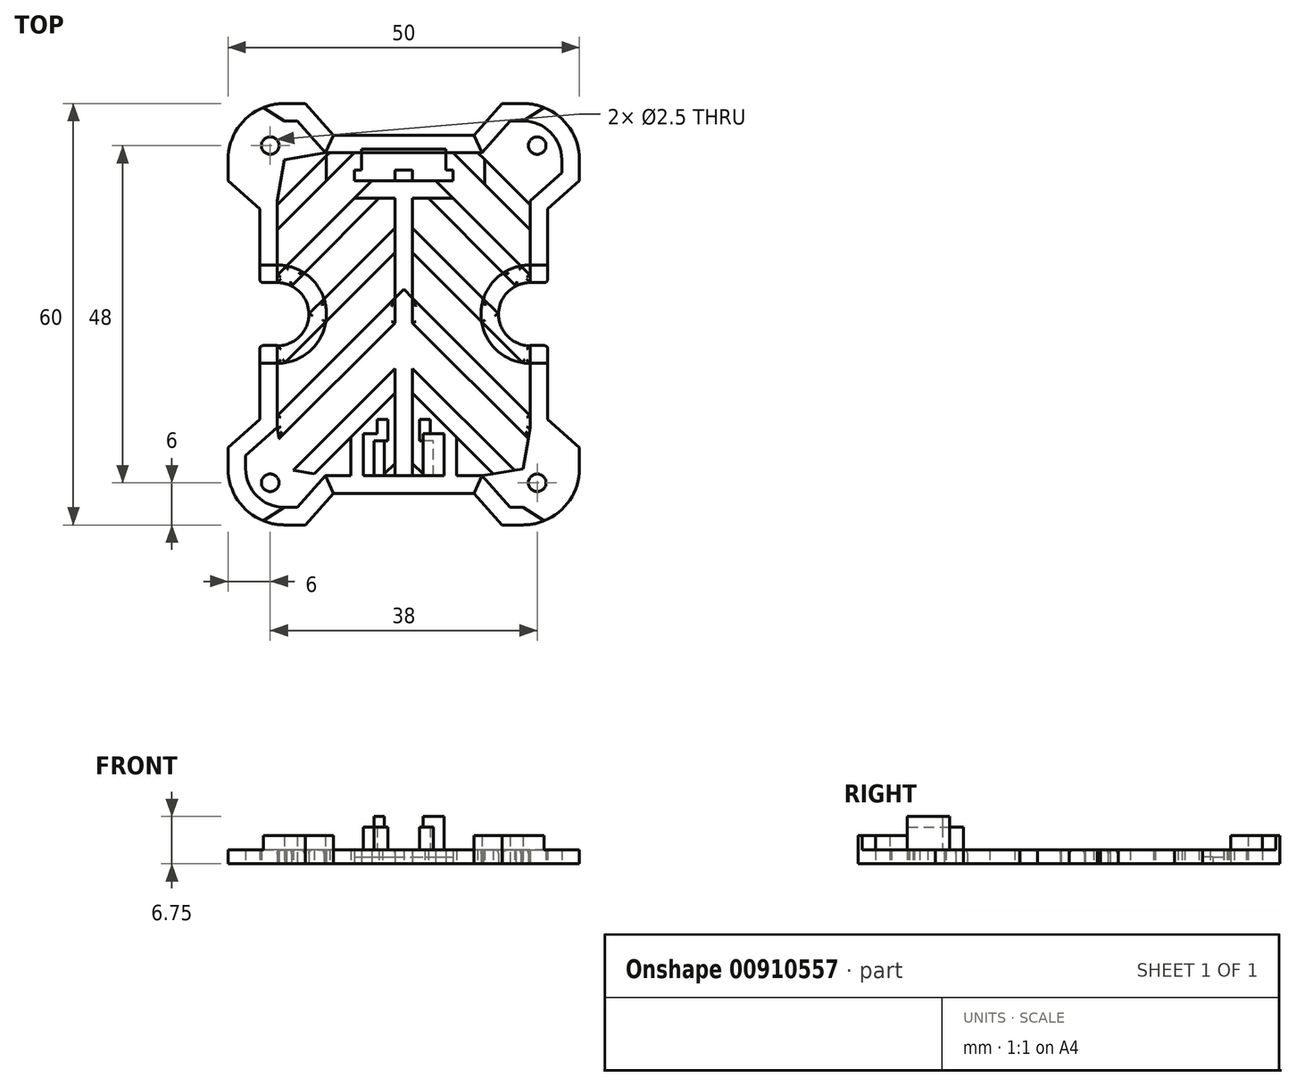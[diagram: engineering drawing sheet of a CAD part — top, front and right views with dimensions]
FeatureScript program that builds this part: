
annotation { "Feature Type Name" : "Feature", "Feature Type Description" : "" }
export const myFeature = defineFeature(function(context is Context, id is Id, definition is map)
    precondition{}
    {
        {
            var Q0;
            Q0=qCreatedBy(makeId("Top.planeOp"),FACE);
            var sketch = newSketch(context, id + "F0", { "sketchPlane" : qUnion([Q0])});
            skPoint(sketch, "E0.visualSharp", {"position": v(-25, 30) * mm});
            skArc(sketch, "E0.filletArc", {"start": v(-17, 30) * mm, "mid": v(-22.66, 27.66) * mm, "end": v(-25, 22) * mm});
            skPoint(sketch, "E1.visualSharp", {"position": v(25, 30) * mm});
            skArc(sketch, "E1.filletArc", {"start": v(25, 22) * mm, "mid": v(22.66, 27.66) * mm, "end": v(17, 30) * mm});
            skPoint(sketch, "E2.visualSharp", {"position": v(25, -30) * mm});
            skArc(sketch, "E2.filletArc", {"start": v(17, -30) * mm, "mid": v(22.66, -27.66) * mm, "end": v(25, -22) * mm});
            skPoint(sketch, "E3.visualSharp", {"position": v(-25, -30) * mm});
            skArc(sketch, "E3.filletArc", {"start": v(-25, -22) * mm, "mid": v(-22.66, -27.66) * mm, "end": v(-17, -30) * mm});
            skCircle(sketch, "E4", {"center": v(-19, 24) * mm, "radius": 1.25 * mm});
            skCircle(sketch, "E5.MirrorC", {"center": v(19, 24) * mm, "radius": 1.25 * mm});
            skCircle(sketch, "E6.MirrorC", {"center": v(19, -24) * mm, "radius": 1.25 * mm});
            skCircle(sketch, "E7.MirrorC", {"center": v(-19, -24) * mm, "radius": 1.25 * mm});
            skLineSegment(sketch, "E8", {"start": v(-10, 25.5) * mm, "end": v(10, 25.5) * mm});
            skLineSegment(sketch, "E9", {"start": v(-17, 30) * mm, "end": v(-14, 30) * mm});
            skLineSegment(sketch, "E10", {"start": v(-10, 25.5) * mm, "end": v(-14, 30) * mm});
            skLineSegment(sketch, "E11", {"start": v(10, 25.5) * mm, "end": v(14, 30) * mm});
            skLineSegment(sketch, "E12", {"start": v(-10, -25.5) * mm, "end": v(10, -25.5) * mm});
            skLineSegment(sketch, "E13", {"start": v(-17, -30) * mm, "end": v(-14, -30) * mm});
            skLineSegment(sketch, "E14", {"start": v(14, 30) * mm, "end": v(17, 30) * mm});
            skLineSegment(sketch, "E15", {"start": v(-14, -30) * mm, "end": v(-10, -25.5) * mm});
            skLineSegment(sketch, "E16", {"start": v(17, -30) * mm, "end": v(14, -30) * mm});
            skLineSegment(sketch, "E17", {"start": v(14, -30) * mm, "end": v(10, -25.5) * mm});
            skLineSegment(sketch, "E18", {"start": v(-25, -22) * mm, "end": v(-25, -19) * mm});
            skLineSegment(sketch, "E19", {"start": v(-25, 22) * mm, "end": v(-25, 19) * mm});
            skLineSegment(sketch, "E20", {"start": v(25, 22) * mm, "end": v(25, 19) * mm});
            skLineSegment(sketch, "E21", {"start": v(25, -22) * mm, "end": v(25, -19) * mm});
            skLineSegment(sketch, "E22", {"start": v(-20.5, -15) * mm, "end": v(-20.5, 15) * mm});
            skLineSegment(sketch, "E23", {"start": v(-25, -19) * mm, "end": v(-20.5, -15) * mm});
            skLineSegment(sketch, "E24", {"start": v(-20.5, 15) * mm, "end": v(-25, 19) * mm});
            skLineSegment(sketch, "E25", {"start": v(20.5, -15) * mm, "end": v(20.5, 15) * mm});
            skLineSegment(sketch, "E26", {"start": v(20.5, 15) * mm, "end": v(25, 19) * mm});
            skLineSegment(sketch, "E27", {"start": v(20.5, -15) * mm, "end": v(25, -19) * mm});
            skLineSegment(sketch, "E28", {"start": v(-10, -25.5) * mm, "end": v(-20.5, -15) * mm, "construction": true});
            skLineSegment(sketch, "E29", {"start": v(10, -25.5) * mm, "end": v(20.5, -15) * mm, "construction": true});
            skLineSegment(sketch, "E30", {"start": v(-20.5, 15) * mm, "end": v(-10, 25.5) * mm, "construction": true});
            skLineSegment(sketch, "E31", {"start": v(20.5, 15) * mm, "end": v(10, 25.5) * mm, "construction": true});
            skLineSegment(sketch, "E32.0", {"start": v(-11.12, 23) * mm, "end": v(-15.12, 27.5) * mm});
            skLineSegment(sketch, "E32.1", {"start": v(17, -27.5) * mm, "end": v(15.12, -27.5) * mm});
            skArc(sketch, "E32.2", {"start": v(17, -27.5) * mm, "mid": v(20.89, -25.89) * mm, "end": v(22.5, -22) * mm});
            skLineSegment(sketch, "E32.3", {"start": v(22.5, -22) * mm, "end": v(22.5, -20.12) * mm});
            skLineSegment(sketch, "E32.4", {"start": v(18, -16.12) * mm, "end": v(22.5, -20.12) * mm});
            skLineSegment(sketch, "E32.5", {"start": v(18, -16.12) * mm, "end": v(18, 16.12) * mm});
            skLineSegment(sketch, "E32.6", {"start": v(18, 16.12) * mm, "end": v(22.5, 20.12) * mm});
            skLineSegment(sketch, "E32.7", {"start": v(11.12, 23) * mm, "end": v(15.12, 27.5) * mm});
            skLineSegment(sketch, "E32.8", {"start": v(15.12, 27.5) * mm, "end": v(17, 27.5) * mm});
            skArc(sketch, "E32.9", {"start": v(22.5, 22) * mm, "mid": v(20.89, 25.89) * mm, "end": v(17, 27.5) * mm});
            skLineSegment(sketch, "E32.10", {"start": v(22.5, 22) * mm, "end": v(22.5, 20.12) * mm});
            skLineSegment(sketch, "E32.11", {"start": v(15.12, -27.5) * mm, "end": v(11.12, -23) * mm});
            skLineSegment(sketch, "E32.12", {"start": v(-11.12, 23) * mm, "end": v(11.12, 23) * mm});
            skLineSegment(sketch, "E32.13", {"start": v(-11.12, -23) * mm, "end": v(11.12, -23) * mm});
            skLineSegment(sketch, "E32.14", {"start": v(-15.12, -27.5) * mm, "end": v(-11.12, -23) * mm});
            skLineSegment(sketch, "E32.15", {"start": v(-17, -27.5) * mm, "end": v(-15.12, -27.5) * mm});
            skArc(sketch, "E32.16", {"start": v(-22.5, -22) * mm, "mid": v(-20.89, -25.89) * mm, "end": v(-17, -27.5) * mm});
            skLineSegment(sketch, "E32.17", {"start": v(-22.5, -22) * mm, "end": v(-22.5, -20.12) * mm});
            skLineSegment(sketch, "E32.18", {"start": v(-22.5, -20.12) * mm, "end": v(-18, -16.12) * mm});
            skLineSegment(sketch, "E32.19", {"start": v(-18, -16.12) * mm, "end": v(-18, 16.12) * mm});
            skLineSegment(sketch, "E32.20", {"start": v(-18, 16.12) * mm, "end": v(-22.5, 20.12) * mm});
            skLineSegment(sketch, "E32.21", {"start": v(-22.5, 22) * mm, "end": v(-22.5, 20.12) * mm});
            skArc(sketch, "E32.22", {"start": v(-17, 27.5) * mm, "mid": v(-20.89, 25.89) * mm, "end": v(-22.5, 22) * mm});
            skLineSegment(sketch, "E32.23", {"start": v(-17, 27.5) * mm, "end": v(-15.12, 27.5) * mm});
            skLineSegment(sketch, "E33", {"start": v(-18, 16.12) * mm, "end": v(-17, 22) * mm});
            skLineSegment(sketch, "E34", {"start": v(-11.12, 23) * mm, "end": v(-17, 22) * mm});
            skLineSegment(sketch, "E35", {"start": v(11.12, 23) * mm, "end": v(17, 22) * mm});
            skLineSegment(sketch, "E36", {"start": v(18, 16.12) * mm, "end": v(17, 22) * mm});
            skLineSegment(sketch, "E37", {"start": v(-11.12, -23) * mm, "end": v(-17, -22) * mm});
            skLineSegment(sketch, "E38", {"start": v(-18, -16.12) * mm, "end": v(-17, -22) * mm});
            skLineSegment(sketch, "E39", {"start": v(11.12, -23) * mm, "end": v(17, -22) * mm});
            skLineSegment(sketch, "E40", {"start": v(18, -16.12) * mm, "end": v(17, -22) * mm});
            skLineSegment(sketch, "E41", {"start": v(0, 3.54) * mm, "end": v(-18, -14.46) * mm});
            skLineSegment(sketch, "E42", {"start": v(0, 3.54) * mm, "end": v(18, -14.46) * mm});
            skLineSegment(sketch, "E43.0", {"start": v(-1.25, -1.25) * mm, "end": v(-17.75, -17.75) * mm});
            skLineSegment(sketch, "E43.1", {"start": v(1.25, -1.25) * mm, "end": v(17.75, -17.75) * mm});
            skLineSegment(sketch, "E44.0.1.0", {"start": v(1.25, 12.29) * mm, "end": v(18, -4.46) * mm});
            skLineSegment(sketch, "E44.0.1.1", {"start": v(1.25, 8.75) * mm, "end": v(18, -8) * mm});
            skLineSegment(sketch, "E44.0.1.2", {"start": v(-1.25, 8.75) * mm, "end": v(-18, -8) * mm});
            skLineSegment(sketch, "E44.0.1.3", {"start": v(-1.25, 12.29) * mm, "end": v(-18, -4.46) * mm});
            skLineSegment(sketch, "E44.0.2.0", {"start": v(1.25, 22.29) * mm, "end": v(18, 5.54) * mm});
            skLineSegment(sketch, "E44.0.2.1", {"start": v(1.25, 18.75) * mm, "end": v(18, 2) * mm});
            skLineSegment(sketch, "E44.0.2.2", {"start": v(-1.25, 18.75) * mm, "end": v(-18, 2) * mm});
            skLineSegment(sketch, "E44.0.2.3", {"start": v(-1.25, 22.29) * mm, "end": v(-18, 5.54) * mm});
            skLineSegment(sketch, "E44.0.3.2", {"start": v(-7, 23) * mm, "end": v(-18, 12) * mm});
            skLineSegment(sketch, "E44.0.3.3", {"start": v(-10.54, 23) * mm, "end": v(-18, 15.54) * mm});
            skLineSegment(sketch, "E44.direction1", {"start": v(18, -14.46) * mm, "end": v(43, -14.46) * mm, "construction": true});
            skLineSegment(sketch, "E44.direction2", {"start": v(18, -14.46) * mm, "end": v(18, -4.46) * mm, "construction": true});
            skLineSegment(sketch, "E45.0.1.0", {"start": v(1.25, -11.25) * mm, "end": v(12.75, -22.75) * mm});
            skLineSegment(sketch, "E45.0.1.1", {"start": v(1.25, -7.71) * mm, "end": v(15.75, -22.21) * mm});
            skLineSegment(sketch, "E45.0.1.2", {"start": v(-1.25, -7.71) * mm, "end": v(-15.75, -22.21) * mm});
            skLineSegment(sketch, "E45.0.1.3", {"start": v(-1.25, -11.25) * mm, "end": v(-12.75, -22.75) * mm});
            skLineSegment(sketch, "E45.0.2.0", {"start": v(1.25, -21.25) * mm, "end": v(3, -23) * mm});
            skLineSegment(sketch, "E45.0.2.1", {"start": v(1.25, -17.71) * mm, "end": v(6.54, -23) * mm});
            skLineSegment(sketch, "E45.0.2.2", {"start": v(-1.25, -17.71) * mm, "end": v(-6.54, -23) * mm});
            skLineSegment(sketch, "E45.0.2.3", {"start": v(-1.25, -21.25) * mm, "end": v(-3, -23) * mm});
            skLineSegment(sketch, "E45.direction1", {"start": v(18, -18) * mm, "end": v(43, -18) * mm, "construction": true});
            skLineSegment(sketch, "E45.direction2", {"start": v(18, -18) * mm, "end": v(18, -28) * mm, "construction": true});
            skPoint(sketch, "E46.orphan", {"position": v(-18, -34.46) * mm});
            skPoint(sketch, "E47.orphan", {"position": v(-18, -38) * mm});
            skPoint(sketch, "E48.orphan", {"position": v(18, -34.46) * mm});
            skLineSegment(sketch, "E49.trimOffspring", {"start": v(7, 23) * mm, "end": v(18, 12) * mm});
            skLineSegment(sketch, "E50.trimOffspring", {"start": v(10.54, 23) * mm, "end": v(18, 15.54) * mm});
            skPoint(sketch, "E51.orphan", {"position": v(0, 30) * mm});
            skPoint(sketch, "E52.orphan", {"position": v(0, 33.54) * mm});
            skPoint(sketch, "E53.orphan", {"position": v(0, 23.54) * mm});
            skLineSegment(sketch, "E54.bottom", {"start": v(-1.25, 23) * mm, "end": v(1.25, 23) * mm});
            skLineSegment(sketch, "E54.top", {"start": v(-1.25, -23) * mm, "end": v(1.25, -23) * mm});
            skLineSegment(sketch, "E54.left", {"start": v(-1.25, 23) * mm, "end": v(-1.25, -23) * mm});
            skLineSegment(sketch, "E54.right", {"start": v(1.25, 23) * mm, "end": v(1.25, -23) * mm});
            skPoint(sketch, "E54.middle", {"position": v(0, 0) * mm});
            skPoint(sketch, "E55.orphan", {"position": v(0, 20) * mm});
            skPoint(sketch, "E56.orphan", {"position": v(0, 13.54) * mm});
            skPoint(sketch, "E57.orphan", {"position": v(0, 10) * mm});
            skPoint(sketch, "E58.orphan", {"position": v(0, -20) * mm});
            skPoint(sketch, "E59.orphan", {"position": v(0, -16.46) * mm});
            skPoint(sketch, "E60.orphan", {"position": v(0, -10) * mm});
            skPoint(sketch, "E61.orphan", {"position": v(0, -6.46) * mm});
            skLineSegment(sketch, "E62", {"start": v(-7.5, -23) * mm, "end": v(-7.5, -17.5) * mm});
            skLineSegment(sketch, "E63.MirrorCS", {"start": v(7.5, -23) * mm, "end": v(7.5, -17.5) * mm});
            skLineSegment(sketch, "E64", {"start": v(-11.12, 23) * mm, "end": v(-10, 25.5) * mm});
            skLineSegment(sketch, "E65", {"start": v(-17, 27.5) * mm, "end": v(-20, 29.42) * mm});
            skLineSegment(sketch, "E66", {"start": v(11.12, 23) * mm, "end": v(10, 25.5) * mm});
            skLineSegment(sketch, "E67", {"start": v(17, 27.5) * mm, "end": v(20, 29.42) * mm});
            skLineSegment(sketch, "E68", {"start": v(-10, -25.5) * mm, "end": v(-11.12, -23) * mm});
            skLineSegment(sketch, "E69", {"start": v(10, -25.5) * mm, "end": v(11.12, -23) * mm});
            skLineSegment(sketch, "E70", {"start": v(-17, -27.5) * mm, "end": v(-20, -29.42) * mm});
            skLineSegment(sketch, "E71", {"start": v(17, -27.5) * mm, "end": v(20, -29.42) * mm});
            skArc(sketch, "E72.trimOffspring", {"start": v(-18, -7) * mm, "mid": v(-11, 0) * mm, "end": v(-18, 7) * mm});
            skArc(sketch, "E73.trimOffspring", {"start": v(-18, -4.5) * mm, "mid": v(-13.5, 0) * mm, "end": v(-18, 4.5) * mm});
            skLineSegment(sketch, "E74", {"start": v(-18, 7) * mm, "end": v(-20.5, 7) * mm});
            skLineSegment(sketch, "E75", {"start": v(-18, 4.5) * mm, "end": v(-20.5, 4.5) * mm});
            skLineSegment(sketch, "E76", {"start": v(-18, -7) * mm, "end": v(-20.5, -7) * mm});
            skLineSegment(sketch, "E77", {"start": v(-18, -4.46) * mm, "end": v(-20.5, -4.46) * mm});
            skArc(sketch, "E78.MirrorCS", {"start": v(18, -4.5) * mm, "mid": v(13.5, 0) * mm, "end": v(18, 4.5) * mm});
            skArc(sketch, "E79.MirrorCS", {"start": v(18, -7) * mm, "mid": v(11, 0) * mm, "end": v(18, 7) * mm});
            skLineSegment(sketch, "E80.MirrorCS", {"start": v(18, 4.5) * mm, "end": v(20.5, 4.5) * mm});
            skLineSegment(sketch, "E81.MirrorCS", {"start": v(18, 7) * mm, "end": v(20.5, 7) * mm});
            skLineSegment(sketch, "E82.MirrorCS", {"start": v(18, -7) * mm, "end": v(20.5, -7) * mm});
            skLineSegment(sketch, "E83.MirrorCS", {"start": v(18, -4.46) * mm, "end": v(20.5, -4.46) * mm});
            skLineSegment(sketch, "E84.bottom", {"start": v(-9, 20.5) * mm, "end": v(-7, 20.5) * mm});
            skLineSegment(sketch, "E84.top", {"start": v(-9, 19) * mm, "end": v(-7, 19) * mm});
            skLineSegment(sketch, "E84.left", {"start": v(-9, 20.5) * mm, "end": v(-9, 19) * mm});
            skLineSegment(sketch, "E84.right", {"start": v(-7, 20.5) * mm, "end": v(-7, 19) * mm});
            skPoint(sketch, "E84.middle", {"position": v(-8, 19.75) * mm});
            skLineSegment(sketch, "E85", {"start": v(-7, 20.5) * mm, "end": v(7, 20.5) * mm});
            skLineSegment(sketch, "E86", {"start": v(-7, 19) * mm, "end": v(7, 19) * mm});
            skLineSegment(sketch, "E87.bottom", {"start": v(7, 20.5) * mm, "end": v(9, 20.5) * mm});
            skLineSegment(sketch, "E87.top", {"start": v(7, 19) * mm, "end": v(9, 19) * mm});
            skLineSegment(sketch, "E87.left", {"start": v(7, 20.5) * mm, "end": v(7, 19) * mm});
            skLineSegment(sketch, "E87.right", {"start": v(9, 20.5) * mm, "end": v(9, 19) * mm});
            skLineSegment(sketch, "E88", {"start": v(7, 19.75) * mm, "end": v(0, 19.75) * mm, "construction": true});
            skLineSegment(sketch, "E89", {"start": v(0, 19.75) * mm, "end": v(-7, 19.75) * mm, "construction": true});
            skLineSegment(sketch, "E90.top", {"start": v(-11, 16.5) * mm, "end": v(11.5, 16.5) * mm});
            skLineSegment(sketch, "E90.left", {"start": v(-11, 23) * mm, "end": v(-11, 16.5) * mm});
            skLineSegment(sketch, "E90.right", {"start": v(11.5, 23) * mm, "end": v(11.5, 16.5) * mm});
            skPoint(sketch, "E90.middle", {"position": v(0, 19.75) * mm});
            skLineSegment(sketch, "E91.bottom", {"start": v(-6, 20.5) * mm, "end": v(6, 20.5) * mm});
            skLineSegment(sketch, "E91.top", {"start": v(-6, 23.5) * mm, "end": v(6, 23.5) * mm});
            skLineSegment(sketch, "E91.left", {"start": v(-6, 20.5) * mm, "end": v(-6, 23.5) * mm});
            skLineSegment(sketch, "E91.right", {"start": v(6, 20.5) * mm, "end": v(6, 23.5) * mm});
            skSolve(sketch);
        }
        {
            var Q0;
            Q0=makeQuery(id+"F0.imprint","IMPRINT",FACE,{"disambiguationData":[TD([[makeQuery(id+"F0.imprint","IMPRINT",EDGE,{"derivedFrom":sQuery(id+"F0.wireOp",EDGE,"qVhlgd7Z-K8wA-2s9c-4Va0-7I31SFR7jzgF.bottom")}),-1.0]])]});
            var Q1;
            {var subQ1=sQuery(id+"F0.wireOp",EDGE,"bAQaguaC-gw7z-6hSp-WNjj-it6Kwomhn3MH.bottom");var subQ4=sQuery(id+"F0.wireOp",EDGE,"bAQaguaC-gw7z-6hSp-WNjj-it6Kwomhn3MH.left");var subQ9=makeQuery(id+"F0.imprint","INTERSECT",VERTEX,{"derivedFrom":[subQ1,subQ4]});Q1=makeQuery(id+"F0.imprint","IMPRINT",FACE,{"disambiguationData":[TD([[makeQuery(id+"F0.imprint","IMPRINT",EDGE,{"disambiguationData":[TD([[subQ9,-1.0]])],"derivedFrom":subQ1}),-1.0]])]});}
            var Q2;
            {var subQ0=sQuery(id+"F0.wireOp",EDGE,"3b41a42e-ea02-44ec-bd11-05c8cb4d84110.MirrorCS");Q2=makeQuery(id+"F0.imprint","IMPRINT",FACE,{"disambiguationData":[TD([[makeQuery(id+"F0.imprint","IMPRINT",EDGE,{"derivedFrom":subQ0}),-1.0]])]});}
            var Q3;
            Q3=makeQuery(id+"F0.imprint","IMPRINT",FACE,{"disambiguationData":[TD([[makeQuery(id+"F0.imprint","IMPRINT",EDGE,{"derivedFrom":sQuery(id+"F0.wireOp",EDGE,"5EblEZfn-I8Wa-IbvZ-PO4Y-9xLoYuIDBuYk.bottom")}),-1.0]])]});
            var Q4;
            {var subQ0=sQuery(id+"F0.wireOp",EDGE,"252a318b-4038-41aa-b63b-639a4f701ae30.MirrorCS");Q4=makeQuery(id+"F0.imprint","IMPRINT",FACE,{"disambiguationData":[TD([[makeQuery(id+"F0.imprint","IMPRINT",EDGE,{"derivedFrom":subQ0}),1.0]])]});}
            var Q5;
            {var subQ0=sQuery(id+"F0.wireOp",EDGE,"58b98b9d-614e-4e5d-8269-9d4372af3b9f0.MirrorCS");Q5=makeQuery(id+"F0.imprint","IMPRINT",FACE,{"disambiguationData":[TD([[makeQuery(id+"F0.imprint","IMPRINT",EDGE,{"derivedFrom":subQ0}),-1.0]])]});}
            var Q6;
            Q6=makeQuery(id+"F0.imprint","IMPRINT",FACE,{"disambiguationData":[TD([[makeQuery(id+"F0.imprint","IMPRINT",EDGE,{"derivedFrom":sQuery(id+"F0.wireOp",EDGE,"E0.filletArc")}),1.0]])]});
            var Q7;
            Q7=makeQuery(id+"F0.imprint","IMPRINT",FACE,{"disambiguationData":[TD([[makeQuery(id+"F0.imprint","IMPRINT",EDGE,{"derivedFrom":sQuery(id+"F0.wireOp",EDGE,"xvgLrtku-wdkR-8HBo-YxuC-FjmSOnXhvL37")}),-1.0]])]});
            var Q8;
            Q8=makeQuery(id+"F0.imprint","IMPRINT",FACE,{"disambiguationData":[TD([[makeQuery(id+"F0.imprint","IMPRINT",EDGE,{"derivedFrom":sQuery(id+"F0.wireOp",EDGE,"E10")}),1.0]])]});
            var Q9;
            Q9=makeQuery(id+"F0.imprint","IMPRINT",FACE,{"disambiguationData":[TD([[makeQuery(id+"F0.imprint","IMPRINT",EDGE,{"derivedFrom":sQuery(id+"F0.wireOp",EDGE,"5909cff1-2e5d-4e63-b456-f55076b46f4d0.MirrorCS")}),-1.0]])]});
            var Q10;
            Q10=makeQuery(id+"F0.imprint","IMPRINT",FACE,{"disambiguationData":[TD([[makeQuery(id+"F0.imprint","IMPRINT",EDGE,{"derivedFrom":sQuery(id+"F0.wireOp",EDGE,"86012b31-d1bc-4a6e-bdbf-ee867ae8a5b00.MirrorCS")}),1.0]])]});
            var Q11;
            Q11=makeQuery(id+"F0.imprint","IMPRINT",FACE,{"disambiguationData":[TD([[makeQuery(id+"F0.imprint","IMPRINT",EDGE,{"derivedFrom":sQuery(id+"F0.wireOp",EDGE,"afaa9ab5-ff9c-4d97-af4b-f4bc579a4ab80.MirrorCS")}),-1.0]])]});
            var Q12;
            {var subQ0=sQuery(id+"F0.wireOp",EDGE,"E49.trimOffspring");Q12=makeQuery(id+"F0.imprint","IMPRINT",FACE,{"disambiguationData":[TD([[makeQuery(id+"F0.imprint","IMPRINT",EDGE,{"derivedFrom":subQ0}),1.0]])]});}
            var Q13;
            {var subQ0=sQuery(id+"F0.wireOp",EDGE,"E45.0.1.1");Q13=makeQuery(id+"F0.imprint","IMPRINT",FACE,{"disambiguationData":[TD([[makeQuery(id+"F0.imprint","IMPRINT",EDGE,{"derivedFrom":subQ0}),-1.0]])]});}
            var Q14;
            {var subQ1=sQuery(id+"F0.wireOp",EDGE,"E45.0.2.0");Q14=makeQuery(id+"F0.imprint","IMPRINT",FACE,{"disambiguationData":[TD([[makeQuery(id+"F0.imprint","IMPRINT",EDGE,{"derivedFrom":subQ1}),1.0]])]});}
            var Q15;
            {var subQ3=sQuery(id+"F0.wireOp",EDGE,"E41");Q15=makeQuery(id+"F0.imprint","IMPRINT",FACE,{"disambiguationData":[TD([[makeQuery(id+"F0.imprint","IMPRINT",EDGE,{"derivedFrom":subQ3}),1.0]])]});}
            var Q16;
            Q16=makeQuery(id+"F0.imprint","IMPRINT",FACE,{"disambiguationData":[TD([[makeQuery(id+"F0.imprint","IMPRINT",EDGE,{"derivedFrom":sQuery(id+"F0.wireOp",EDGE,"E6.MirrorC")}),-1.0]])]});
            var Q17;
            Q17=makeQuery(id+"F0.imprint","IMPRINT",FACE,{"disambiguationData":[TD([[makeQuery(id+"F0.imprint","IMPRINT",EDGE,{"derivedFrom":sQuery(id+"F0.wireOp",EDGE,"E5.MirrorC")}),1.0]])]});
            var Q18;
            Q18=makeQuery(id+"F0.imprint","IMPRINT",FACE,{"disambiguationData":[TD([[makeQuery(id+"F0.imprint","IMPRINT",EDGE,{"derivedFrom":sQuery(id+"F0.wireOp",EDGE,"E4")}),-1.0]])]});
            var Q19;
            Q19=makeQuery(id+"F0.imprint","IMPRINT",FACE,{"disambiguationData":[TD([[makeQuery(id+"F0.imprint","IMPRINT",EDGE,{"derivedFrom":sQuery(id+"F0.wireOp",EDGE,"E7.MirrorC")}),1.0]])]});
            var Q20;
            {var subQ13=sQuery(id+"F0.wireOp",EDGE,"E54.top");Q20=makeQuery(id+"F0.imprint","IMPRINT",FACE,{"disambiguationData":[TD([[makeQuery(id+"F0.imprint","IMPRINT",EDGE,{"derivedFrom":subQ13}),1.0]])]});}
            var Q21;
            {var subQ5=sQuery(id+"F0.wireOp",EDGE,"E42");var subQ6=sQuery(id+"F0.wireOp",EDGE,"E32.5");var subQ7=makeQuery(id+"F0.imprint","INTERSECT",VERTEX,{"derivedFrom":[subQ6,subQ5]});Q21=makeQuery(id+"F0.imprint","IMPRINT",FACE,{"disambiguationData":[TD([[makeQuery(id+"F0.imprint","IMPRINT",EDGE,{"disambiguationData":[TD([[subQ7,1.0]])],"derivedFrom":subQ5}),-1.0]])]});}
            var Q22;
            {var subQ0=sQuery(id+"F0.wireOp",EDGE,"E45.0.1.2");Q22=makeQuery(id+"F0.imprint","IMPRINT",FACE,{"disambiguationData":[TD([[makeQuery(id+"F0.imprint","IMPRINT",EDGE,{"derivedFrom":subQ0}),1.0]])]});}
            var Q23;
            {var subQ0=sQuery(id+"F0.wireOp",EDGE,"E45.0.2.2");Q23=makeQuery(id+"F0.imprint","IMPRINT",FACE,{"disambiguationData":[TD([[makeQuery(id+"F0.imprint","IMPRINT",EDGE,{"derivedFrom":subQ0}),1.0]])]});}
            var Q24;
            {var subQ0=sQuery(id+"F0.wireOp",EDGE,"E45.0.2.3");Q24=makeQuery(id+"F0.imprint","IMPRINT",FACE,{"disambiguationData":[TD([[makeQuery(id+"F0.imprint","IMPRINT",EDGE,{"derivedFrom":subQ0}),1.0]])]});}
            var Q25;
            {var subQ0=sQuery(id+"F0.wireOp",EDGE,"E45.0.2.0");Q25=makeQuery(id+"F0.imprint","IMPRINT",FACE,{"disambiguationData":[TD([[makeQuery(id+"F0.imprint","IMPRINT",EDGE,{"derivedFrom":subQ0}),-1.0]])]});}
            var Q26;
            {var subQ4=sQuery(id+"F0.wireOp",EDGE,"E45.0.2.1");Q26=makeQuery(id+"F0.imprint","IMPRINT",FACE,{"disambiguationData":[TD([[makeQuery(id+"F0.imprint","IMPRINT",EDGE,{"derivedFrom":subQ4}),1.0]])]});}
            var Q27;
            {var subQ4=sQuery(id+"F0.wireOp",EDGE,"E45.0.2.2");Q27=makeQuery(id+"F0.imprint","IMPRINT",FACE,{"disambiguationData":[TD([[makeQuery(id+"F0.imprint","IMPRINT",EDGE,{"derivedFrom":subQ4}),-1.0]])]});}
            var Q28;
            {var subQ11=sQuery(id+"F0.wireOp",EDGE,"E18");Q28=makeQuery(id+"F0.imprint","IMPRINT",FACE,{"disambiguationData":[TD([[makeQuery(id+"F0.imprint","IMPRINT",EDGE,{"derivedFrom":subQ11}),-1.0]])]});}
            var Q29;
            Q29=makeQuery(id+"F0.imprint","IMPRINT",FACE,{"disambiguationData":[TD([[makeQuery(id+"F0.imprint","IMPRINT",EDGE,{"derivedFrom":sQuery(id+"F0.wireOp",EDGE,"E8")}),-1.0]])]});
            var Q30;
            {var subQ0=sQuery(id+"F0.wireOp",EDGE,"E20");Q30=makeQuery(id+"F0.imprint","IMPRINT",FACE,{"disambiguationData":[TD([[makeQuery(id+"F0.imprint","IMPRINT",EDGE,{"derivedFrom":subQ0}),-1.0]])]});}
            var Q31;
            Q31=makeQuery(id+"F0.imprint","IMPRINT",FACE,{"disambiguationData":[TD([[makeQuery(id+"F0.imprint","IMPRINT",EDGE,{"derivedFrom":sQuery(id+"F0.wireOp",EDGE,"E12")}),1.0]])]});
            var Q32;
            Q32=makeQuery(id+"F0.imprint","IMPRINT",FACE,{"disambiguationData":[TD([[makeQuery(id+"F0.imprint","IMPRINT",EDGE,{"derivedFrom":sQuery(id+"F0.wireOp",EDGE,"E11")}),-1.0]])]});
            var Q33;
            {var subQ0=sQuery(id+"F0.wireOp",EDGE,"E16");Q33=makeQuery(id+"F0.imprint","IMPRINT",FACE,{"disambiguationData":[TD([[makeQuery(id+"F0.imprint","IMPRINT",EDGE,{"derivedFrom":subQ0}),-1.0]])]});}
            var Q34;
            {var subQ0=sQuery(id+"F0.wireOp",EDGE,"E13");Q34=makeQuery(id+"F0.imprint","IMPRINT",FACE,{"disambiguationData":[TD([[makeQuery(id+"F0.imprint","IMPRINT",EDGE,{"derivedFrom":subQ0}),1.0]])]});}
            var Q35;
            {var subQ3=sQuery(id+"F0.wireOp",EDGE,"E19");Q35=makeQuery(id+"F0.imprint","IMPRINT",FACE,{"disambiguationData":[TD([[makeQuery(id+"F0.imprint","IMPRINT",EDGE,{"derivedFrom":subQ3}),1.0]])]});}
            var Q36;
            {var subQ4=sQuery(id+"F0.wireOp",EDGE,"E21");Q36=makeQuery(id+"F0.imprint","IMPRINT",FACE,{"disambiguationData":[TD([[makeQuery(id+"F0.imprint","IMPRINT",EDGE,{"derivedFrom":subQ4}),1.0]])]});}
            var Q37;
            {var subQ0=sQuery(id+"F0.wireOp",EDGE,"E82.MirrorCS");Q37=makeQuery(id+"F0.imprint","IMPRINT",FACE,{"disambiguationData":[TD([[makeQuery(id+"F0.imprint","IMPRINT",EDGE,{"derivedFrom":subQ0}),1.0]])]});}
            var Q38;
            {var subQ0=sQuery(id+"F0.wireOp",EDGE,"E44.0.2.0");var subQ1=sQuery(id+"F0.wireOp",EDGE,"E32.5");var subQ2=makeQuery(id+"F0.imprint","INTERSECT",VERTEX,{"derivedFrom":[subQ1,subQ0]});Q38=makeQuery(id+"F0.imprint","IMPRINT",FACE,{"disambiguationData":[TD([[makeQuery(id+"F0.imprint","IMPRINT",EDGE,{"disambiguationData":[TD([[subQ2,1.0]])],"derivedFrom":subQ0}),1.0]])]});}
            var Q39;
            {var subQ1=sQuery(id+"F0.wireOp",EDGE,"E32.5");var subQ7=sQuery(id+"F0.wireOp",EDGE,"E44.0.2.0");var subQ8=makeQuery(id+"F0.imprint","INTERSECT",VERTEX,{"derivedFrom":[subQ1,subQ7]});Q39=makeQuery(id+"F0.imprint","IMPRINT",FACE,{"disambiguationData":[TD([[makeQuery(id+"F0.imprint","IMPRINT",EDGE,{"disambiguationData":[TD([[subQ8,1.0]])],"derivedFrom":subQ7}),-1.0]])]});}
            var Q40;
            {var subQ0=sQuery(id+"F0.wireOp",EDGE,"E79.MirrorCS");var subQ1=sQuery(id+"F0.wireOp",EDGE,"E44.0.1.0");var subQ2=makeQuery(id+"F0.imprint","INTERSECT",VERTEX,{"derivedFrom":[subQ1,subQ0]});Q40=makeQuery(id+"F0.imprint","IMPRINT",FACE,{"disambiguationData":[TD([[makeQuery(id+"F0.imprint","IMPRINT",EDGE,{"disambiguationData":[TD([[subQ2,-1.0]])],"derivedFrom":subQ1}),1.0]])]});}
            var Q41;
            {var subQ3=sQuery(id+"F0.wireOp",EDGE,"E44.0.1.0");var subQ5=sQuery(id+"F0.wireOp",EDGE,"E79.MirrorCS");var subQ9=makeQuery(id+"F0.imprint","INTERSECT",VERTEX,{"derivedFrom":[subQ3,subQ5]});Q41=makeQuery(id+"F0.imprint","IMPRINT",FACE,{"disambiguationData":[TD([[makeQuery(id+"F0.imprint","IMPRINT",EDGE,{"disambiguationData":[TD([[subQ9,-1.0]])],"derivedFrom":subQ3}),-1.0]])]});}
            var Q42;
            {var subQ0=sQuery(id+"F0.wireOp",EDGE,"E79.MirrorCS");var subQ1=sQuery(id+"F0.wireOp",EDGE,"E44.0.1.1");var subQ2=makeQuery(id+"F0.imprint","INTERSECT",VERTEX,{"disambiguationData":[OD(0.0)],"derivedFrom":[subQ1,subQ0]});Q42=makeQuery(id+"F0.imprint","IMPRINT",FACE,{"disambiguationData":[TD([[makeQuery(id+"F0.imprint","IMPRINT",EDGE,{"disambiguationData":[TD([[subQ2,-1.0]])],"derivedFrom":subQ1}),-1.0]])]});}
            var Q43;
            {var subQ0=sQuery(id+"F0.wireOp",EDGE,"E80.MirrorCS");Q43=makeQuery(id+"F0.imprint","IMPRINT",FACE,{"disambiguationData":[TD([[makeQuery(id+"F0.imprint","IMPRINT",EDGE,{"derivedFrom":subQ0}),1.0]])]});}
            var Q44;
            {var subQ0=sQuery(id+"F0.wireOp",EDGE,"E54.right");var subQ1=sQuery(id+"F0.wireOp",EDGE,"E44.0.1.0");var subQ2=makeQuery(id+"F0.imprint","INTERSECT",VERTEX,{"derivedFrom":[subQ1,subQ0]});Q44=makeQuery(id+"F0.imprint","IMPRINT",FACE,{"disambiguationData":[TD([[makeQuery(id+"F0.imprint","IMPRINT",EDGE,{"disambiguationData":[TD([[subQ2,-1.0]])],"derivedFrom":subQ1}),-1.0]])]});}
            var Q45;
            {var subQ0=sQuery(id+"F0.wireOp",EDGE,"E72.trimOffspring");var subQ1=sQuery(id+"F0.wireOp",EDGE,"E44.0.1.3");var subQ2=makeQuery(id+"F0.imprint","INTERSECT",VERTEX,{"derivedFrom":[subQ1,subQ0]});Q45=makeQuery(id+"F0.imprint","IMPRINT",FACE,{"disambiguationData":[TD([[makeQuery(id+"F0.imprint","IMPRINT",EDGE,{"disambiguationData":[TD([[subQ2,-1.0]])],"derivedFrom":subQ1}),-1.0]])]});}
            var Q46;
            {var subQ0=sQuery(id+"F0.wireOp",EDGE,"E74");Q46=makeQuery(id+"F0.imprint","IMPRINT",FACE,{"disambiguationData":[TD([[makeQuery(id+"F0.imprint","IMPRINT",EDGE,{"derivedFrom":subQ0}),1.0]])]});}
            var Q47;
            {var subQ0=sQuery(id+"F0.wireOp",EDGE,"E54.left");var subQ1=sQuery(id+"F0.wireOp",EDGE,"E44.0.1.2");var subQ2=makeQuery(id+"F0.imprint","INTERSECT",VERTEX,{"derivedFrom":[subQ1,subQ0]});Q47=makeQuery(id+"F0.imprint","IMPRINT",FACE,{"disambiguationData":[TD([[makeQuery(id+"F0.imprint","IMPRINT",EDGE,{"disambiguationData":[TD([[subQ2,-1.0]])],"derivedFrom":subQ1}),-1.0]])]});}
            var Q48;
            {var subQ0=sQuery(id+"F0.wireOp",EDGE,"E44.0.2.3");var subQ1=sQuery(id+"F0.wireOp",EDGE,"E32.19");var subQ2=makeQuery(id+"F0.imprint","INTERSECT",VERTEX,{"derivedFrom":[subQ1,subQ0]});Q48=makeQuery(id+"F0.imprint","IMPRINT",FACE,{"disambiguationData":[TD([[makeQuery(id+"F0.imprint","IMPRINT",EDGE,{"disambiguationData":[TD([[subQ2,1.0]])],"derivedFrom":subQ0}),-1.0]])]});}
            var Q49;
            {var subQ0=sQuery(id+"F0.wireOp",EDGE,"E72.trimOffspring");var subQ1=sQuery(id+"F0.wireOp",EDGE,"E44.0.1.2");var subQ2=makeQuery(id+"F0.imprint","INTERSECT",VERTEX,{"disambiguationData":[OD(0.0)],"derivedFrom":[subQ1,subQ0]});Q49=makeQuery(id+"F0.imprint","IMPRINT",FACE,{"disambiguationData":[TD([[makeQuery(id+"F0.imprint","IMPRINT",EDGE,{"disambiguationData":[TD([[subQ2,-1.0]])],"derivedFrom":subQ1}),1.0]])]});}
            var Q50;
            {var subQ0=sQuery(id+"F0.wireOp",EDGE,"E72.trimOffspring");var subQ1=sQuery(id+"F0.wireOp",EDGE,"E44.0.2.2");var subQ2=makeQuery(id+"F0.imprint","INTERSECT",VERTEX,{"derivedFrom":[subQ1,subQ0]});Q50=makeQuery(id+"F0.imprint","IMPRINT",FACE,{"disambiguationData":[TD([[makeQuery(id+"F0.imprint","IMPRINT",EDGE,{"disambiguationData":[TD([[subQ2,-1.0]])],"derivedFrom":subQ1}),-1.0]])]});}
            var Q51;
            {var subQ0=sQuery(id+"F0.wireOp",EDGE,"E72.trimOffspring");var subQ3=sQuery(id+"F0.wireOp",EDGE,"E44.0.1.2");var subQ10=makeQuery(id+"F0.imprint","INTERSECT",VERTEX,{"disambiguationData":[OD(0.0)],"derivedFrom":[subQ3,subQ0]});Q51=makeQuery(id+"F0.imprint","IMPRINT",FACE,{"disambiguationData":[TD([[makeQuery(id+"F0.imprint","IMPRINT",EDGE,{"disambiguationData":[TD([[subQ10,-1.0]])],"derivedFrom":subQ3}),-1.0]])]});}
            var Q52;
            {var subQ0=sQuery(id+"F0.wireOp",EDGE,"E76");Q52=makeQuery(id+"F0.imprint","IMPRINT",FACE,{"disambiguationData":[TD([[makeQuery(id+"F0.imprint","IMPRINT",EDGE,{"derivedFrom":subQ0}),-1.0]])]});}
            var Q53;
            {var subQ0=sQuery(id+"F0.wireOp",EDGE,"E90.top");var subQ1=sQuery(id+"F0.wireOp",EDGE,"E44.0.2.2");var subQ2=makeQuery(id+"F0.imprint","INTERSECT",VERTEX,{"derivedFrom":[subQ1,subQ0]});Q53=makeQuery(id+"F0.imprint","IMPRINT",FACE,{"disambiguationData":[TD([[makeQuery(id+"F0.imprint","IMPRINT",EDGE,{"disambiguationData":[TD([[subQ2,-1.0]])],"derivedFrom":subQ1}),-1.0]])]});}
            var Q54;
            {var subQ0=sQuery(id+"F0.wireOp",EDGE,"E90.top");var subQ1=sQuery(id+"F0.wireOp",EDGE,"E44.0.2.0");var subQ2=makeQuery(id+"F0.imprint","INTERSECT",VERTEX,{"derivedFrom":[subQ1,subQ0]});Q54=makeQuery(id+"F0.imprint","IMPRINT",FACE,{"disambiguationData":[TD([[makeQuery(id+"F0.imprint","IMPRINT",EDGE,{"disambiguationData":[TD([[subQ2,-1.0]])],"derivedFrom":subQ1}),-1.0]])]});}
            var Q55;
            {var subQ0=sQuery(id+"F0.wireOp",EDGE,"E49.trimOffspring");var subQ1=sQuery(id+"F0.wireOp",EDGE,"E32.5");var subQ2=makeQuery(id+"F0.imprint","INTERSECT",VERTEX,{"derivedFrom":[subQ1,subQ0]});Q55=makeQuery(id+"F0.imprint","IMPRINT",FACE,{"disambiguationData":[TD([[makeQuery(id+"F0.imprint","IMPRINT",EDGE,{"disambiguationData":[TD([[subQ2,-1.0]])],"derivedFrom":subQ1}),1.0]])]});}
            var Q56;
            {var subQ0=sQuery(id+"F0.wireOp",EDGE,"E44.0.3.2");var subQ1=sQuery(id+"F0.wireOp",EDGE,"E32.19");var subQ2=makeQuery(id+"F0.imprint","INTERSECT",VERTEX,{"derivedFrom":[subQ1,subQ0]});Q56=makeQuery(id+"F0.imprint","IMPRINT",FACE,{"disambiguationData":[TD([[makeQuery(id+"F0.imprint","IMPRINT",EDGE,{"disambiguationData":[TD([[subQ2,-1.0]])],"derivedFrom":subQ1}),-1.0]])]});}
            var Q57;
            {var subQ0=sQuery(id+"F0.wireOp",EDGE,"E87.top");Q57=makeQuery(id+"F0.imprint","IMPRINT",FACE,{"disambiguationData":[TD([[makeQuery(id+"F0.imprint","IMPRINT",EDGE,{"derivedFrom":subQ0}),-1.0]])]});}
            var Q58;
            {var subQ3=sQuery(id+"F0.wireOp",EDGE,"E86");var subQ5=sQuery(id+"F0.wireOp",EDGE,"E44.0.2.0");var subQ6=makeQuery(id+"F0.imprint","INTERSECT",VERTEX,{"derivedFrom":[subQ5,subQ3]});Q58=makeQuery(id+"F0.imprint","IMPRINT",FACE,{"disambiguationData":[TD([[makeQuery(id+"F0.imprint","IMPRINT",EDGE,{"disambiguationData":[TD([[subQ6,-1.0]])],"derivedFrom":subQ5}),-1.0]])]});}
            var Q59;
            {var subQ1=sQuery(id+"F0.wireOp",EDGE,"E32.12");var subQ6=sQuery(id+"F0.wireOp",EDGE,"E44.0.3.2");var subQ9=makeQuery(id+"F0.imprint","INTERSECT",VERTEX,{"derivedFrom":[subQ1,subQ6]});Q59=makeQuery(id+"F0.imprint","IMPRINT",FACE,{"disambiguationData":[TD([[makeQuery(id+"F0.imprint","IMPRINT",EDGE,{"disambiguationData":[TD([[subQ9,1.0]])],"derivedFrom":subQ1}),-1.0]])]});}
            var Q60;
            {var subQ0=sQuery(id+"F0.wireOp",EDGE,"E84.top");Q60=makeQuery(id+"F0.imprint","IMPRINT",FACE,{"disambiguationData":[TD([[makeQuery(id+"F0.imprint","IMPRINT",EDGE,{"derivedFrom":subQ0}),-1.0]])]});}
            var Q61;
            {var subQ3=sQuery(id+"F0.wireOp",EDGE,"E54.left");var subQ6=sQuery(id+"F0.wireOp",EDGE,"E44.0.2.2");var subQ9=makeQuery(id+"F0.imprint","INTERSECT",VERTEX,{"derivedFrom":[subQ6,subQ3]});Q61=makeQuery(id+"F0.imprint","IMPRINT",FACE,{"disambiguationData":[TD([[makeQuery(id+"F0.imprint","IMPRINT",EDGE,{"disambiguationData":[TD([[subQ9,-1.0]])],"derivedFrom":subQ6}),-1.0]])]});}
            var Q62;
            {var subQ4=sQuery(id+"F0.wireOp",EDGE,"E54.left");var subQ5=makeQuery(id+"F0.imprint","INTERSECT",VERTEX,{"derivedFrom":[sQuery(id+"F0.wireOp",EDGE,"E44.0.2.2"),subQ4]});Q62=makeQuery(id+"F0.imprint","IMPRINT",FACE,{"disambiguationData":[TD([[makeQuery(id+"F0.imprint","IMPRINT",EDGE,{"disambiguationData":[TD([[subQ5,1.0]])],"derivedFrom":subQ4}),1.0]])]});}
            var Q63;
            {var subQ3=sQuery(id+"F0.wireOp",EDGE,"E42");var subQ4=sQuery(id+"F0.wireOp",EDGE,"E41");var subQ5=makeQuery(id+"F0.imprint","INTERSECT",VERTEX,{"derivedFrom":[subQ4,subQ3]});Q63=makeQuery(id+"F0.imprint","IMPRINT",FACE,{"disambiguationData":[TD([[makeQuery(id+"F0.imprint","IMPRINT",EDGE,{"disambiguationData":[TD([[subQ5,-1.0]])],"derivedFrom":subQ4}),-1.0]])]});}
            var Q64;
            {var subQ0=sQuery(id+"F0.wireOp",EDGE,"E54.left");var subQ1=sQuery(id+"F0.wireOp",EDGE,"E44.0.2.2");var subQ2=makeQuery(id+"F0.imprint","INTERSECT",VERTEX,{"derivedFrom":[subQ1,subQ0]});Q64=makeQuery(id+"F0.imprint","IMPRINT",FACE,{"disambiguationData":[TD([[makeQuery(id+"F0.imprint","IMPRINT",EDGE,{"disambiguationData":[TD([[subQ2,-1.0]])],"derivedFrom":subQ1}),1.0]])]});}
            var Q65;
            {var subQ0=sQuery(id+"F0.wireOp",EDGE,"E54.right");var subQ1=sQuery(id+"F0.wireOp",EDGE,"E44.0.2.1");var subQ2=makeQuery(id+"F0.imprint","INTERSECT",VERTEX,{"derivedFrom":[subQ1,subQ0]});Q65=makeQuery(id+"F0.imprint","IMPRINT",FACE,{"disambiguationData":[TD([[makeQuery(id+"F0.imprint","IMPRINT",EDGE,{"disambiguationData":[TD([[subQ2,-1.0]])],"derivedFrom":subQ1}),-1.0]])]});}
            extrude(context, id + "F1", {"entities" : qUnion([Q0, Q1, Q2, Q3, Q4, Q5, Q6, Q7, Q8, Q9, Q10, Q11, Q12, Q13, Q14, Q15, Q16, Q17, Q18, Q19, Q20, Q21, Q22, Q23, Q24, Q25, Q26, Q27, Q28, Q29, Q30, Q31, Q32, Q33, Q34, Q35, Q36, Q37, Q38, Q39, Q40, Q41, Q42, Q43, Q44, Q45, Q46, Q47, Q48, Q49, Q50, Q51, Q52, Q53, Q54, Q55, Q56, Q57, Q58, Q59, Q60, Q61, Q62, Q63, Q64, Q65]), "depth" : 2 * mm});
        }
        {
            var Q0;
            {var subQ5=sQuery(id+"F0.wireOp",EDGE,"E84.right");Q0=makeQuery(id+"F0.imprint","IMPRINT",FACE,{"disambiguationData":[TD([[makeQuery(id+"F0.imprint","IMPRINT",EDGE,{"derivedFrom":subQ5}),1.0]])]});}
            var Q1;
            {var subQ0=sQuery(id+"F0.wireOp",EDGE,"E85");var subQ1=sQuery(id+"F0.wireOp",EDGE,"E44.0.2.3");var subQ2=makeQuery(id+"F0.imprint","INTERSECT",VERTEX,{"derivedFrom":[subQ1,subQ0]});Q1=makeQuery(id+"F0.imprint","IMPRINT",FACE,{"disambiguationData":[TD([[makeQuery(id+"F0.imprint","IMPRINT",EDGE,{"disambiguationData":[TD([[subQ2,-1.0]])],"derivedFrom":subQ1}),1.0]])]});}
            var Q2;
            {var subQ0=sQuery(id+"F0.wireOp",EDGE,"E85");var subQ1=sQuery(id+"F0.wireOp",EDGE,"E44.0.2.0");var subQ2=makeQuery(id+"F0.imprint","INTERSECT",VERTEX,{"derivedFrom":[subQ1,subQ0]});Q2=makeQuery(id+"F0.imprint","IMPRINT",FACE,{"disambiguationData":[TD([[makeQuery(id+"F0.imprint","IMPRINT",EDGE,{"disambiguationData":[TD([[subQ2,-1.0]])],"derivedFrom":subQ1}),-1.0]])]});}
            var Q3;
            {var subQ5=sQuery(id+"F0.wireOp",EDGE,"E87.left");Q3=makeQuery(id+"F0.imprint","IMPRINT",FACE,{"disambiguationData":[TD([[makeQuery(id+"F0.imprint","IMPRINT",EDGE,{"derivedFrom":subQ5}),-1.0]])]});}
            var Q4;
            {var subQ0=sQuery(id+"F0.wireOp",EDGE,"E91.bottom");var subQ1=sQuery(id+"F0.wireOp",EDGE,"E44.0.2.3");var subQ2=makeQuery(id+"F0.imprint","INTERSECT",VERTEX,{"derivedFrom":[subQ1,subQ0]});Q4=makeQuery(id+"F0.imprint","IMPRINT",FACE,{"disambiguationData":[TD([[makeQuery(id+"F0.imprint","IMPRINT",EDGE,{"disambiguationData":[TD([[subQ2,-1.0]])],"derivedFrom":subQ1}),1.0]])]});}
            var Q5;
            {var subQ0=sQuery(id+"F0.wireOp",EDGE,"E91.bottom");var subQ1=sQuery(id+"F0.wireOp",EDGE,"E54.left");var subQ2=makeQuery(id+"F0.imprint","INTERSECT",VERTEX,{"derivedFrom":[subQ1,subQ0]});Q5=makeQuery(id+"F0.imprint","IMPRINT",FACE,{"disambiguationData":[TD([[makeQuery(id+"F0.imprint","IMPRINT",EDGE,{"disambiguationData":[TD([[subQ2,-1.0]])],"derivedFrom":subQ1}),1.0]])]});}
            var Q6;
            {var subQ0=sQuery(id+"F0.wireOp",EDGE,"E91.bottom");var subQ1=sQuery(id+"F0.wireOp",EDGE,"E44.0.2.0");var subQ2=makeQuery(id+"F0.imprint","INTERSECT",VERTEX,{"derivedFrom":[subQ1,subQ0]});Q6=makeQuery(id+"F0.imprint","IMPRINT",FACE,{"disambiguationData":[TD([[makeQuery(id+"F0.imprint","IMPRINT",EDGE,{"disambiguationData":[TD([[subQ2,-1.0]])],"derivedFrom":subQ1}),-1.0]])]});}
            var Q7;
            {var subQ0=sQuery(id+"F0.wireOp",EDGE,"E54.right");var subQ1=sQuery(id+"F0.wireOp",EDGE,"E44.0.2.0");var subQ2=makeQuery(id+"F0.imprint","INTERSECT",VERTEX,{"derivedFrom":[subQ1,subQ0]});Q7=makeQuery(id+"F0.imprint","IMPRINT",FACE,{"disambiguationData":[TD([[makeQuery(id+"F0.imprint","IMPRINT",EDGE,{"disambiguationData":[TD([[subQ2,-1.0]])],"derivedFrom":subQ1}),1.0]])]});}
            var Q8;
            {var subQ1=sQuery(id+"F0.wireOp",EDGE,"E54.bottom");Q8=makeQuery(id+"F0.imprint","IMPRINT",FACE,{"disambiguationData":[TD([[makeQuery(id+"F0.imprint","IMPRINT",EDGE,{"derivedFrom":subQ1}),1.0]])]});}
            var Q9;
            {var subQ3=sQuery(id+"F0.wireOp",EDGE,"E44.0.2.3");var subQ5=sQuery(id+"F0.wireOp",EDGE,"E54.left");var subQ6=makeQuery(id+"F0.imprint","INTERSECT",VERTEX,{"derivedFrom":[subQ3,subQ5]});Q9=makeQuery(id+"F0.imprint","IMPRINT",FACE,{"disambiguationData":[TD([[makeQuery(id+"F0.imprint","IMPRINT",EDGE,{"disambiguationData":[TD([[subQ6,-1.0]])],"derivedFrom":subQ3}),-1.0]])]});}
            var Q10;
            {var subQ2=sQuery(id+"F0.wireOp",EDGE,"E54.bottom");Q10=makeQuery(id+"F0.imprint","IMPRINT",FACE,{"disambiguationData":[TD([[makeQuery(id+"F0.imprint","IMPRINT",EDGE,{"derivedFrom":subQ2}),-1.0]])]});}
            extrude(context, id + "F2", {"entities" : qUnion([Q0, Q1, Q2, Q3, Q4, Q5, Q6, Q7, Q8, Q9, Q10]), "operationType" : NewBodyOperationType.ADD, "depth" : 1 * mm});
        }
        {
            var Q0;
            {var subQ0=sQuery(id+"F0.wireOp",EDGE,"E91.right");var subQ1=sQuery(id+"F0.wireOp",EDGE,"E91.left");var subQ2=sQuery(id+"F0.wireOp",EDGE,"E91.top");var subQ3=sQuery(id+"F0.wireOp",EDGE,"E86");var subQ4=sQuery(id+"F0.wireOp",EDGE,"E85");Q0=makeQuery(id+"F2.boolean.opBoolean","MERGE",FACE,{"derivedFrom":[makeQuery(id+"F1.opExtrude","CAP_FACE",FACE,{"disambiguationData":[OSD([sQuery(id+"F0.wireOp",EDGE,"E0.filletArc"),sQuery(id+"F0.wireOp",EDGE,"E1.filletArc"),sQuery(id+"F0.wireOp",EDGE,"E2.filletArc"),sQuery(id+"F0.wireOp",EDGE,"E3.filletArc"),sQuery(id+"F0.wireOp",EDGE,"E4"),sQuery(id+"F0.wireOp",EDGE,"E5.MirrorC"),sQuery(id+"F0.wireOp",EDGE,"E6.MirrorC"),sQuery(id+"F0.wireOp",EDGE,"E7.MirrorC"),sQuery(id+"F0.wireOp",EDGE,"E8"),sQuery(id+"F0.wireOp",EDGE,"E9"),sQuery(id+"F0.wireOp",EDGE,"E10"),sQuery(id+"F0.wireOp",EDGE,"E11"),sQuery(id+"F0.wireOp",EDGE,"E12"),sQuery(id+"F0.wireOp",EDGE,"E13"),sQuery(id+"F0.wireOp",EDGE,"E14"),sQuery(id+"F0.wireOp",EDGE,"E15"),sQuery(id+"F0.wireOp",EDGE,"E16"),sQuery(id+"F0.wireOp",EDGE,"E17"),sQuery(id+"F0.wireOp",EDGE,"E18"),sQuery(id+"F0.wireOp",EDGE,"E19"),sQuery(id+"F0.wireOp",EDGE,"E20"),sQuery(id+"F0.wireOp",EDGE,"E21"),sQuery(id+"F0.wireOp",EDGE,"E22"),sQuery(id+"F0.wireOp",EDGE,"E23"),sQuery(id+"F0.wireOp",EDGE,"E24"),sQuery(id+"F0.wireOp",EDGE,"E25"),sQuery(id+"F0.wireOp",EDGE,"E26"),sQuery(id+"F0.wireOp",EDGE,"E27"),sQuery(id+"F0.wireOp",EDGE,"E32.5"),sQuery(id+"F0.wireOp",EDGE,"E32.12"),sQuery(id+"F0.wireOp",EDGE,"E32.13"),sQuery(id+"F0.wireOp",EDGE,"E32.19"),sQuery(id+"F0.wireOp",EDGE,"E33"),sQuery(id+"F0.wireOp",EDGE,"E34"),sQuery(id+"F0.wireOp",EDGE,"E35"),sQuery(id+"F0.wireOp",EDGE,"E36"),sQuery(id+"F0.wireOp",EDGE,"E37"),sQuery(id+"F0.wireOp",EDGE,"E38"),sQuery(id+"F0.wireOp",EDGE,"E39"),sQuery(id+"F0.wireOp",EDGE,"E40"),sQuery(id+"F0.wireOp",EDGE,"E41"),sQuery(id+"F0.wireOp",EDGE,"E42"),sQuery(id+"F0.wireOp",EDGE,"E43.0"),sQuery(id+"F0.wireOp",EDGE,"E43.1"),sQuery(id+"F0.wireOp",EDGE,"E44.0.1.0"),sQuery(id+"F0.wireOp",EDGE,"E44.0.1.1"),sQuery(id+"F0.wireOp",EDGE,"E44.0.1.2"),sQuery(id+"F0.wireOp",EDGE,"E44.0.1.3"),sQuery(id+"F0.wireOp",EDGE,"E44.0.2.0"),sQuery(id+"F0.wireOp",EDGE,"E44.0.2.1"),sQuery(id+"F0.wireOp",EDGE,"E44.0.2.2"),sQuery(id+"F0.wireOp",EDGE,"E44.0.2.3"),sQuery(id+"F0.wireOp",EDGE,"E44.0.3.2"),sQuery(id+"F0.wireOp",EDGE,"E44.0.3.3"),sQuery(id+"F0.wireOp",EDGE,"E45.0.1.0"),sQuery(id+"F0.wireOp",EDGE,"E45.0.1.1"),sQuery(id+"F0.wireOp",EDGE,"E45.0.1.2"),sQuery(id+"F0.wireOp",EDGE,"E45.0.1.3"),sQuery(id+"F0.wireOp",EDGE,"E49.trimOffspring"),sQuery(id+"F0.wireOp",EDGE,"E50.trimOffspring"),sQuery(id+"F0.wireOp",EDGE,"E54.left"),sQuery(id+"F0.wireOp",EDGE,"E54.right"),sQuery(id+"F0.wireOp",EDGE,"E62"),sQuery(id+"F0.wireOp",EDGE,"E63.MirrorCS"),sQuery(id+"F0.wireOp",EDGE,"E72.trimOffspring"),sQuery(id+"F0.wireOp",EDGE,"E73.trimOffspring"),sQuery(id+"F0.wireOp",EDGE,"E75"),sQuery(id+"F0.wireOp",EDGE,"E77"),sQuery(id+"F0.wireOp",EDGE,"E78.MirrorCS"),sQuery(id+"F0.wireOp",EDGE,"E79.MirrorCS"),sQuery(id+"F0.wireOp",EDGE,"E80.MirrorCS"),sQuery(id+"F0.wireOp",EDGE,"E83.MirrorCS"),sQuery(id+"F0.wireOp",EDGE,"E84.bottom"),sQuery(id+"F0.wireOp",EDGE,"E84.top"),sQuery(id+"F0.wireOp",EDGE,"E84.left"),subQ4,subQ3,sQuery(id+"F0.wireOp",EDGE,"E87.bottom"),sQuery(id+"F0.wireOp",EDGE,"E87.top"),sQuery(id+"F0.wireOp",EDGE,"E87.right"),sQuery(id+"F0.wireOp",EDGE,"E90.top"),sQuery(id+"F0.wireOp",EDGE,"E90.left"),sQuery(id+"F0.wireOp",EDGE,"E90.right"),subQ2,subQ1,subQ0])],"isStart":true}),makeQuery(id+"F2.opExtrude","CAP_FACE",FACE,{"disambiguationData":[OSD([sQuery(id+"F0.wireOp",EDGE,"E84.right"),subQ4,subQ3,sQuery(id+"F0.wireOp",EDGE,"E87.left"),subQ2,subQ1,subQ0])],"isStart":true})]});}
            var Q1;
            Q1=makeQuery(id+"F7.boolean.opBoolean","MERGE",FACE,{"derivedFrom":[makeQuery(id+"F5.opExtrude","SWEPT_FACE",FACE,{"disambiguationData":[OSD([sQuery(id+"F4.wireOp",EDGE,"E92.bottom")])]}),makeQuery(id+"F7.opExtrude","SWEPT_FACE",FACE,{"disambiguationData":[OSD([sQuery(id+"F6.wireOp",EDGE,"E123.MirrorCS")])]})]});
            var Q2;
            Q2=makeQuery(id+"F7.boolean.opBoolean","MERGE",FACE,{"derivedFrom":[makeQuery(id+"F5.opExtrude","SWEPT_FACE",FACE,{"disambiguationData":[OSD([sQuery(id+"F4.wireOp",EDGE,"E92.left")])]}),makeQuery(id+"F7.opExtrude","SWEPT_FACE",FACE,{"disambiguationData":[OSD([sQuery(id+"F6.wireOp",EDGE,"E122.MirrorCS")])]})]});
            var Q3;
            Q3=makeQuery(id+"F7.boolean.opBoolean","MERGE",FACE,{"derivedFrom":[makeQuery(id+"F5.opExtrude","SWEPT_FACE",FACE,{"disambiguationData":[OSD([sQuery(id+"F4.wireOp",EDGE,"E104.MirrorCS")])]}),makeQuery(id+"F7.opExtrude","SWEPT_FACE",FACE,{"disambiguationData":[OSD([sQuery(id+"F6.wireOp",EDGE,"E120.MirrorCS")])]})]});
            var Q4;
            Q4=makeQuery(id+"F7.opExtrude","CAP_FACE",FACE,{"disambiguationData":[OSD([sQuery(id+"F6.wireOp",EDGE,"E117.MirrorCS"),sQuery(id+"F6.wireOp",EDGE,"E118.MirrorCS"),sQuery(id+"F6.wireOp",EDGE,"E119.MirrorCS"),sQuery(id+"F6.wireOp",EDGE,"E120.MirrorCS")])],"isStart":false});
            var Q5;
            Q5=makeQuery(id+"F2.opExtrude","CAP_FACE",FACE,{"disambiguationData":[OSD([sQuery(id+"F0.wireOp",EDGE,"E84.right"),sQuery(id+"F0.wireOp",EDGE,"E85"),sQuery(id+"F0.wireOp",EDGE,"E86"),sQuery(id+"F0.wireOp",EDGE,"E87.left"),sQuery(id+"F0.wireOp",EDGE,"E91.top"),sQuery(id+"F0.wireOp",EDGE,"E91.left"),sQuery(id+"F0.wireOp",EDGE,"E91.right")])],"isStart":false});
            var Q6;
            Q6=makeQuery(id+"F1.opExtrude","CAP_EDGE",EDGE,{"disambiguationData":[OSD([sQuery(id+"F0.wireOp",EDGE,"E91.left")])],"isStart":false});
            var Q7;
            Q7=makeQuery(id+"F1.opExtrude","CAP_EDGE",EDGE,{"disambiguationData":[OSD([sQuery(id+"F0.wireOp",EDGE,"E84.bottom"),sQuery(id+"F0.wireOp",EDGE,"E85")])],"isStart":false});
            var Q8;
            Q8=makeQuery(id+"F1.opExtrude","CAP_EDGE",EDGE,{"disambiguationData":[OSD([sQuery(id+"F0.wireOp",EDGE,"E84.left")])],"isStart":false});
            var Q9;
            Q9=makeQuery(id+"F1.opExtrude","CAP_EDGE",EDGE,{"disambiguationData":[OSD([sQuery(id+"F0.wireOp",EDGE,"E84.top"),sQuery(id+"F0.wireOp",EDGE,"E86"),sQuery(id+"F0.wireOp",EDGE,"E87.top")])],"isStart":false});
            var Q10;
            Q10=makeQuery(id+"F1.opExtrude","CAP_EDGE",EDGE,{"disambiguationData":[OSD([sQuery(id+"F0.wireOp",EDGE,"E91.top")])],"isStart":false});
            var Q11;
            Q11=makeQuery(id+"F1.opExtrude","CAP_EDGE",EDGE,{"disambiguationData":[OSD([sQuery(id+"F0.wireOp",EDGE,"E85"),sQuery(id+"F0.wireOp",EDGE,"E87.bottom")])],"isStart":false});
            var Q12;
            Q12=makeQuery(id+"F1.opExtrude","CAP_EDGE",EDGE,{"disambiguationData":[OSD([sQuery(id+"F0.wireOp",EDGE,"E91.right")])],"isStart":false});
            var Q13;
            Q13=makeQuery(id+"F1.opExtrude","CAP_EDGE",EDGE,{"disambiguationData":[OSD([sQuery(id+"F0.wireOp",EDGE,"E87.right")])],"isStart":false});
            var Q14;
            Q14=makeQuery(id+"F1.opExtrude","SWEPT_EDGE",EDGE,{"disambiguationData":[OSD([sQuery(id+"F0.wireOp",EDGE,"E25"),sQuery(id+"F0.wireOp",EDGE,"E80.MirrorCS")])]});
            var Q15;
            Q15=makeQuery(id+"F1.opExtrude","SWEPT_EDGE",EDGE,{"disambiguationData":[OSD([sQuery(id+"F0.wireOp",EDGE,"E25"),sQuery(id+"F0.wireOp",EDGE,"E83.MirrorCS")])]});
            var Q16;
            Q16=makeQuery(id+"F1.opExtrude","SWEPT_EDGE",EDGE,{"disambiguationData":[OSD([sQuery(id+"F0.wireOp",EDGE,"E22"),sQuery(id+"F0.wireOp",EDGE,"E77")])]});
            var Q17;
            Q17=makeQuery(id+"F1.opExtrude","SWEPT_EDGE",EDGE,{"disambiguationData":[OSD([sQuery(id+"F0.wireOp",EDGE,"E22"),sQuery(id+"F0.wireOp",EDGE,"E75")])]});
            var Q18;
            Q18=makeQuery(id+"F1.opExtrude","CAP_EDGE",EDGE,{"disambiguationData":[OSD([sQuery(id+"F0.wireOp",EDGE,"E73.trimOffspring")])],"isStart":false});
            var Q19;
            Q19=makeQuery(id+"F1.opExtrude","CAP_EDGE",EDGE,{"disambiguationData":[OSD([sQuery(id+"F0.wireOp",EDGE,"E78.MirrorCS")])],"isStart":false});
            var Q20;
            Q20=makeQuery(id+"F1.opExtrude","CAP_FACE",FACE,{"disambiguationData":[OSD([sQuery(id+"F0.wireOp",EDGE,"E0.filletArc"),sQuery(id+"F0.wireOp",EDGE,"E1.filletArc"),sQuery(id+"F0.wireOp",EDGE,"E2.filletArc"),sQuery(id+"F0.wireOp",EDGE,"E3.filletArc"),sQuery(id+"F0.wireOp",EDGE,"E4"),sQuery(id+"F0.wireOp",EDGE,"E5.MirrorC"),sQuery(id+"F0.wireOp",EDGE,"E6.MirrorC"),sQuery(id+"F0.wireOp",EDGE,"E7.MirrorC"),sQuery(id+"F0.wireOp",EDGE,"E8"),sQuery(id+"F0.wireOp",EDGE,"E9"),sQuery(id+"F0.wireOp",EDGE,"E10"),sQuery(id+"F0.wireOp",EDGE,"E11"),sQuery(id+"F0.wireOp",EDGE,"E12"),sQuery(id+"F0.wireOp",EDGE,"E13"),sQuery(id+"F0.wireOp",EDGE,"E14"),sQuery(id+"F0.wireOp",EDGE,"E15"),sQuery(id+"F0.wireOp",EDGE,"E16"),sQuery(id+"F0.wireOp",EDGE,"E17"),sQuery(id+"F0.wireOp",EDGE,"E18"),sQuery(id+"F0.wireOp",EDGE,"E19"),sQuery(id+"F0.wireOp",EDGE,"E20"),sQuery(id+"F0.wireOp",EDGE,"E21"),sQuery(id+"F0.wireOp",EDGE,"E22"),sQuery(id+"F0.wireOp",EDGE,"E23"),sQuery(id+"F0.wireOp",EDGE,"E24"),sQuery(id+"F0.wireOp",EDGE,"E25"),sQuery(id+"F0.wireOp",EDGE,"E26"),sQuery(id+"F0.wireOp",EDGE,"E27"),sQuery(id+"F0.wireOp",EDGE,"E32.5"),sQuery(id+"F0.wireOp",EDGE,"E32.12"),sQuery(id+"F0.wireOp",EDGE,"E32.13"),sQuery(id+"F0.wireOp",EDGE,"E32.19"),sQuery(id+"F0.wireOp",EDGE,"E33"),sQuery(id+"F0.wireOp",EDGE,"E34"),sQuery(id+"F0.wireOp",EDGE,"E35"),sQuery(id+"F0.wireOp",EDGE,"E36"),sQuery(id+"F0.wireOp",EDGE,"E37"),sQuery(id+"F0.wireOp",EDGE,"E38"),sQuery(id+"F0.wireOp",EDGE,"E39"),sQuery(id+"F0.wireOp",EDGE,"E40"),sQuery(id+"F0.wireOp",EDGE,"E41"),sQuery(id+"F0.wireOp",EDGE,"E42"),sQuery(id+"F0.wireOp",EDGE,"E43.0"),sQuery(id+"F0.wireOp",EDGE,"E43.1"),sQuery(id+"F0.wireOp",EDGE,"E44.0.1.0"),sQuery(id+"F0.wireOp",EDGE,"E44.0.1.1"),sQuery(id+"F0.wireOp",EDGE,"E44.0.1.2"),sQuery(id+"F0.wireOp",EDGE,"E44.0.1.3"),sQuery(id+"F0.wireOp",EDGE,"E44.0.2.0"),sQuery(id+"F0.wireOp",EDGE,"E44.0.2.1"),sQuery(id+"F0.wireOp",EDGE,"E44.0.2.2"),sQuery(id+"F0.wireOp",EDGE,"E44.0.2.3"),sQuery(id+"F0.wireOp",EDGE,"E44.0.3.2"),sQuery(id+"F0.wireOp",EDGE,"E44.0.3.3"),sQuery(id+"F0.wireOp",EDGE,"E45.0.1.0"),sQuery(id+"F0.wireOp",EDGE,"E45.0.1.1"),sQuery(id+"F0.wireOp",EDGE,"E45.0.1.2"),sQuery(id+"F0.wireOp",EDGE,"E45.0.1.3"),sQuery(id+"F0.wireOp",EDGE,"E49.trimOffspring"),sQuery(id+"F0.wireOp",EDGE,"E50.trimOffspring"),sQuery(id+"F0.wireOp",EDGE,"E54.left"),sQuery(id+"F0.wireOp",EDGE,"E54.right"),sQuery(id+"F0.wireOp",EDGE,"E62"),sQuery(id+"F0.wireOp",EDGE,"E63.MirrorCS"),sQuery(id+"F0.wireOp",EDGE,"E72.trimOffspring"),sQuery(id+"F0.wireOp",EDGE,"E73.trimOffspring"),sQuery(id+"F0.wireOp",EDGE,"E75"),sQuery(id+"F0.wireOp",EDGE,"E77"),sQuery(id+"F0.wireOp",EDGE,"E78.MirrorCS"),sQuery(id+"F0.wireOp",EDGE,"E79.MirrorCS"),sQuery(id+"F0.wireOp",EDGE,"E80.MirrorCS"),sQuery(id+"F0.wireOp",EDGE,"E83.MirrorCS"),sQuery(id+"F0.wireOp",EDGE,"E84.bottom"),sQuery(id+"F0.wireOp",EDGE,"E84.top"),sQuery(id+"F0.wireOp",EDGE,"E84.left"),sQuery(id+"F0.wireOp",EDGE,"E85"),sQuery(id+"F0.wireOp",EDGE,"E86"),sQuery(id+"F0.wireOp",EDGE,"E87.bottom"),sQuery(id+"F0.wireOp",EDGE,"E87.top"),sQuery(id+"F0.wireOp",EDGE,"E87.right"),sQuery(id+"F0.wireOp",EDGE,"E90.top"),sQuery(id+"F0.wireOp",EDGE,"E90.left"),sQuery(id+"F0.wireOp",EDGE,"E90.right"),sQuery(id+"F0.wireOp",EDGE,"E91.top"),sQuery(id+"F0.wireOp",EDGE,"E91.left"),sQuery(id+"F0.wireOp",EDGE,"E91.right")])],"isStart":false});
            fillet(context, id + "F3", {"entities" : qUnion([Q0, Q1, Q2, Q3, Q4, Q5, Q6, Q7, Q8, Q9, Q10, Q11, Q12, Q13, Q14, Q15, Q16, Q17, Q18, Q19, Q20]), "radius" : .5 * mm, "tangentPropagation" : true, "allowEdgeOverflow" : false});
        }
        {
            var Q0;
            Q0=makeQuery(id+"F1.opExtrude","CAP_FACE",FACE,{"disambiguationData":[OSD([sQuery(id+"F0.wireOp",EDGE,"E0.filletArc"),sQuery(id+"F0.wireOp",EDGE,"E1.filletArc"),sQuery(id+"F0.wireOp",EDGE,"E2.filletArc"),sQuery(id+"F0.wireOp",EDGE,"E3.filletArc"),sQuery(id+"F0.wireOp",EDGE,"E4"),sQuery(id+"F0.wireOp",EDGE,"E5.MirrorC"),sQuery(id+"F0.wireOp",EDGE,"E6.MirrorC"),sQuery(id+"F0.wireOp",EDGE,"E7.MirrorC"),sQuery(id+"F0.wireOp",EDGE,"E8"),sQuery(id+"F0.wireOp",EDGE,"E9"),sQuery(id+"F0.wireOp",EDGE,"E10"),sQuery(id+"F0.wireOp",EDGE,"E11"),sQuery(id+"F0.wireOp",EDGE,"E12"),sQuery(id+"F0.wireOp",EDGE,"E13"),sQuery(id+"F0.wireOp",EDGE,"E14"),sQuery(id+"F0.wireOp",EDGE,"E15"),sQuery(id+"F0.wireOp",EDGE,"E16"),sQuery(id+"F0.wireOp",EDGE,"E17"),sQuery(id+"F0.wireOp",EDGE,"E18"),sQuery(id+"F0.wireOp",EDGE,"E19"),sQuery(id+"F0.wireOp",EDGE,"E20"),sQuery(id+"F0.wireOp",EDGE,"E21"),sQuery(id+"F0.wireOp",EDGE,"E22"),sQuery(id+"F0.wireOp",EDGE,"E23"),sQuery(id+"F0.wireOp",EDGE,"E24"),sQuery(id+"F0.wireOp",EDGE,"E25"),sQuery(id+"F0.wireOp",EDGE,"E26"),sQuery(id+"F0.wireOp",EDGE,"E27"),sQuery(id+"F0.wireOp",EDGE,"E32.5"),sQuery(id+"F0.wireOp",EDGE,"E32.12"),sQuery(id+"F0.wireOp",EDGE,"E32.13"),sQuery(id+"F0.wireOp",EDGE,"E32.19"),sQuery(id+"F0.wireOp",EDGE,"E33"),sQuery(id+"F0.wireOp",EDGE,"E34"),sQuery(id+"F0.wireOp",EDGE,"E35"),sQuery(id+"F0.wireOp",EDGE,"E36"),sQuery(id+"F0.wireOp",EDGE,"E37"),sQuery(id+"F0.wireOp",EDGE,"E38"),sQuery(id+"F0.wireOp",EDGE,"E39"),sQuery(id+"F0.wireOp",EDGE,"E40"),sQuery(id+"F0.wireOp",EDGE,"E41"),sQuery(id+"F0.wireOp",EDGE,"E42"),sQuery(id+"F0.wireOp",EDGE,"E43.0"),sQuery(id+"F0.wireOp",EDGE,"E43.1"),sQuery(id+"F0.wireOp",EDGE,"E44.0.1.0"),sQuery(id+"F0.wireOp",EDGE,"E44.0.1.1"),sQuery(id+"F0.wireOp",EDGE,"E44.0.1.2"),sQuery(id+"F0.wireOp",EDGE,"E44.0.1.3"),sQuery(id+"F0.wireOp",EDGE,"E44.0.2.0"),sQuery(id+"F0.wireOp",EDGE,"E44.0.2.1"),sQuery(id+"F0.wireOp",EDGE,"E44.0.2.2"),sQuery(id+"F0.wireOp",EDGE,"E44.0.2.3"),sQuery(id+"F0.wireOp",EDGE,"E44.0.3.2"),sQuery(id+"F0.wireOp",EDGE,"E44.0.3.3"),sQuery(id+"F0.wireOp",EDGE,"E45.0.1.0"),sQuery(id+"F0.wireOp",EDGE,"E45.0.1.1"),sQuery(id+"F0.wireOp",EDGE,"E45.0.1.2"),sQuery(id+"F0.wireOp",EDGE,"E45.0.1.3"),sQuery(id+"F0.wireOp",EDGE,"E45.0.2.1"),sQuery(id+"F0.wireOp",EDGE,"E45.0.2.2"),sQuery(id+"F0.wireOp",EDGE,"E49.trimOffspring"),sQuery(id+"F0.wireOp",EDGE,"E50.trimOffspring"),sQuery(id+"F0.wireOp",EDGE,"E54.left"),sQuery(id+"F0.wireOp",EDGE,"E54.right")])],"isStart":false});
            var sketch = newSketch(context, id + "F4", { "sketchPlane" : qUnion([Q0])});
            skLineSegment(sketch, "E92.bottom", {"start": v(5.75, -23) * mm, "end": v(5.75, -17) * mm});
            skLineSegment(sketch, "E92.top", {"start": v(4.25, -23) * mm, "end": v(4.25, -18) * mm});
            skLineSegment(sketch, "E92.left", {"start": v(5.75, -23) * mm, "end": v(4.25, -23) * mm});
            skLineSegment(sketch, "E92.right", {"start": v(5.75, -17) * mm, "end": v(4.25, -17) * mm});
            skLineSegment(sketch, "E93.left", {"start": v(4.25, -18) * mm, "end": v(3.75, -18) * mm});
            skLineSegment(sketch, "E93.right", {"start": v(4.25, -17) * mm, "end": v(3.75, -17) * mm});
            skLineSegment(sketch, "E94.bottom", {"start": v(3.75, -17) * mm, "end": v(3.75, -15) * mm});
            skLineSegment(sketch, "E94.top", {"start": v(2.25, -18) * mm, "end": v(2.25, -15) * mm});
            skLineSegment(sketch, "E94.left", {"start": v(3.75, -18) * mm, "end": v(2.25, -18) * mm});
            skLineSegment(sketch, "E94.right", {"start": v(3.75, -15) * mm, "end": v(2.25, -15) * mm});
            skPoint(sketch, "E95.visualSharp", {"position": v(3.75, -15) * mm});
            skPoint(sketch, "E96.visualSharp", {"position": v(2.25, -15) * mm});
            skPoint(sketch, "E97.visualSharp", {"position": v(2.25, -18) * mm});
            skPoint(sketch, "E98.visualSharp", {"position": v(4.25, -23) * mm});
            skPoint(sketch, "E99", {"position": v(5.75, -23) * mm});
            skPoint(sketch, "E100", {"position": v(5.75, -17) * mm});
            skLineSegment(sketch, "E101", {"start": v(2.25, -15) * mm, "end": v(-2.25, -15) * mm, "construction": true});
            skPoint(sketch, "E102", {"position": v(0, -15) * mm});
            skLineSegment(sketch, "E103", {"start": v(0, -15) * mm, "end": v(0, -25.74) * mm, "construction": true});
            skLineSegment(sketch, "E104.MirrorCS", {"start": v(-5.75, -23) * mm, "end": v(-4.25, -23) * mm});
            skLineSegment(sketch, "E105.MirrorCS", {"start": v(-5.75, -23) * mm, "end": v(-5.75, -17) * mm});
            skLineSegment(sketch, "E106.MirrorCS", {"start": v(-4.25, -17) * mm, "end": v(-3.75, -17) * mm});
            skLineSegment(sketch, "E107.MirrorCS", {"start": v(-5.75, -17) * mm, "end": v(-4.25, -17) * mm});
            skLineSegment(sketch, "E108.MirrorCS", {"start": v(-3.75, -18) * mm, "end": v(-2.25, -18) * mm});
            skLineSegment(sketch, "E109.MirrorCS", {"start": v(-2.25, -18) * mm, "end": v(-2.25, -15) * mm});
            skLineSegment(sketch, "E110.MirrorCS", {"start": v(-3.75, -15) * mm, "end": v(-2.25, -15) * mm});
            skLineSegment(sketch, "E111.MirrorCS", {"start": v(-4.25, -23) * mm, "end": v(-4.25, -18) * mm});
            skLineSegment(sketch, "E112.MirrorCS", {"start": v(-4.25, -18) * mm, "end": v(-3.75, -18) * mm});
            skLineSegment(sketch, "E113.MirrorCS", {"start": v(-3.75, -17) * mm, "end": v(-3.75, -15) * mm});
            skSolve(sketch);
        }
        {
            var Q0;
            Q0=makeQuery(id+"F4.imprint","IMPRINT",FACE,{"disambiguationData":[TD([[makeQuery(id+"F4.imprint","IMPRINT",EDGE,{"derivedFrom":sQuery(id+"F4.wireOp",EDGE,"082e3635-987c-4050-8474-c287f25c8af8.MirrorCS")}),1.0]])]});
            var Q1;
            Q1=makeQuery(id+"F4.imprint","IMPRINT",FACE,{"disambiguationData":[TD([[makeQuery(id+"F4.imprint","IMPRINT",EDGE,{"derivedFrom":sQuery(id+"F4.wireOp",EDGE,"E92.bottom")}),1.0]])]});
            var Q2;
            Q2=makeQuery(id+"F4.imprint","IMPRINT",FACE,{"disambiguationData":[TD([[makeQuery(id+"F4.imprint","IMPRINT",EDGE,{"derivedFrom":sQuery(id+"F4.wireOp",EDGE,"E104.MirrorCS")}),1.0]])]});
            extrude(context, id + "F5", {"entities" : qUnion([Q0, Q1, Q2]), "operationType" : NewBodyOperationType.ADD, "depth" : 3.25 * mm});
        }
        {
            var Q0;
            Q0=makeQuery(id+"F5.opExtrude","CAP_FACE",FACE,{"disambiguationData":[OSD([sQuery(id+"F4.wireOp",EDGE,"E104.MirrorCS"),sQuery(id+"F4.wireOp",EDGE,"E105.MirrorCS"),sQuery(id+"F4.wireOp",EDGE,"E106.MirrorCS"),sQuery(id+"F4.wireOp",EDGE,"E107.MirrorCS"),sQuery(id+"F4.wireOp",EDGE,"E108.MirrorCS"),sQuery(id+"F4.wireOp",EDGE,"E109.MirrorCS"),sQuery(id+"F4.wireOp",EDGE,"E110.MirrorCS"),sQuery(id+"F4.wireOp",EDGE,"E111.MirrorCS"),sQuery(id+"F4.wireOp",EDGE,"E112.MirrorCS"),sQuery(id+"F4.wireOp",EDGE,"E113.MirrorCS")])],"isStart":false});
            var sketch = newSketch(context, id + "F6", { "sketchPlane" : qUnion([Q0])});
            skLineSegment(sketch, "E114", {"start": v(2.75, -17) * mm, "end": v(-2.75, -17) * mm, "construction": true});
            skPoint(sketch, "E115", {"position": v(0, -17) * mm});
            skLineSegment(sketch, "E116", {"start": v(0, -17) * mm, "end": v(0, -22.48) * mm, "construction": true});
            skLineSegment(sketch, "E117.MirrorCS", {"start": v(-2.75, -23) * mm, "end": v(-2.75, -17) * mm});
            skLineSegment(sketch, "E118.MirrorCS", {"start": v(-5.75, -17) * mm, "end": v(-2.75, -17) * mm});
            skLineSegment(sketch, "E119.MirrorCS", {"start": v(-5.75, -23) * mm, "end": v(-5.75, -17) * mm});
            skLineSegment(sketch, "E120.MirrorCS", {"start": v(-5.75, -23) * mm, "end": v(-2.75, -23) * mm});
            skLineSegment(sketch, "E121.MirrorCS", {"start": v(2.75, -23) * mm, "end": v(2.75, -17) * mm});
            skLineSegment(sketch, "E122.MirrorCS", {"start": v(5.75, -23) * mm, "end": v(2.75, -23) * mm});
            skLineSegment(sketch, "E123.MirrorCS", {"start": v(5.75, -23) * mm, "end": v(5.75, -17) * mm});
            skLineSegment(sketch, "E124.MirrorCS", {"start": v(5.75, -17) * mm, "end": v(2.75, -17) * mm});
            skSolve(sketch);
        }
        {
            var Q0;
            Q0=makeQuery(id+"F6.imprint","IMPRINT",FACE,{"disambiguationData":[TD([[makeQuery(id+"F6.imprint","IMPRINT",EDGE,{"derivedFrom":sQuery(id+"F6.wireOp",EDGE,"E119.MirrorCS")}),-1.0]])]});
            var Q1;
            {var subQ1=sQuery(id+"F6.wireOp",EDGE,"ee415b56-a3a5-43e7-b2b9-08c54a094791.MirrorCS");Q1=makeQuery(id+"F6.imprint","IMPRINT",FACE,{"disambiguationData":[TD([[makeQuery(id+"F6.imprint","IMPRINT",EDGE,{"derivedFrom":subQ1}),-1.0]])]});}
            var Q2;
            Q2=makeQuery(id+"F6.imprint","IMPRINT",FACE,{"disambiguationData":[TD([[makeQuery(id+"F6.imprint","IMPRINT",EDGE,{"derivedFrom":sQuery(id+"F6.wireOp",EDGE,"4d7947e5-259c-42fd-9370-be67d3335575.bottom")}),1.0]])]});
            var Q3;
            {var subQ5=makeQuery(id+"F5.opExtrude","CAP_EDGE",EDGE,{"disambiguationData":[OSD([sQuery(id+"F4.wireOp",EDGE,"E111.MirrorCS")])],"isStart":false});Q3=makeQuery(id+"F6.imprint","IMPRINT",FACE,{"disambiguationData":[TD([[makeQuery(id+"F6.imprint","IMPRINT",EDGE,{"derivedFrom":subQ5}),-1.0]])]});}
            var Q4;
            Q4=makeQuery(id+"F6.imprint","IMPRINT",FACE,{"disambiguationData":[TD([[makeQuery(id+"F6.imprint","IMPRINT",EDGE,{"derivedFrom":sQuery(id+"F6.wireOp",EDGE,"E121.MirrorCS")}),-1.0]])]});
            extrude(context, id + "F7", {"entities" : qUnion([Q0, Q1, Q2, Q3, Q4]), "operationType" : NewBodyOperationType.ADD, "depth" : 1.5 * mm});
        }
        {
            var Q0;
            {var subQ0=sQuery(id+"F0.wireOp",EDGE,"E9");Q0=makeQuery(id+"F0.imprint","IMPRINT",FACE,{"disambiguationData":[TD([[makeQuery(id+"F0.imprint","IMPRINT",EDGE,{"derivedFrom":subQ0}),-1.0]])]});}
            var Q1;
            Q1=makeQuery(id+"F0.imprint","IMPRINT",FACE,{"disambiguationData":[TD([[makeQuery(id+"F0.imprint","IMPRINT",EDGE,{"derivedFrom":sQuery(id+"F0.wireOp",EDGE,"E11")}),-1.0]])]});
            var Q2;
            {var subQ0=sQuery(id+"F0.wireOp",EDGE,"E16");Q2=makeQuery(id+"F0.imprint","IMPRINT",FACE,{"disambiguationData":[TD([[makeQuery(id+"F0.imprint","IMPRINT",EDGE,{"derivedFrom":subQ0}),-1.0]])]});}
            var Q3;
            {var subQ0=sQuery(id+"F0.wireOp",EDGE,"E13");Q3=makeQuery(id+"F0.imprint","IMPRINT",FACE,{"disambiguationData":[TD([[makeQuery(id+"F0.imprint","IMPRINT",EDGE,{"derivedFrom":subQ0}),1.0]])]});}
            extrude(context, id + "F8", {"entities" : qUnion([Q0, Q1, Q2, Q3]), "operationType" : NewBodyOperationType.ADD, "depth" : 4 * mm, "hasSecondDirection" : true, "secondDirectionOppositeDirection" : false, "secondDirectionDepth" : 1.5 * mm});
        }
    });
